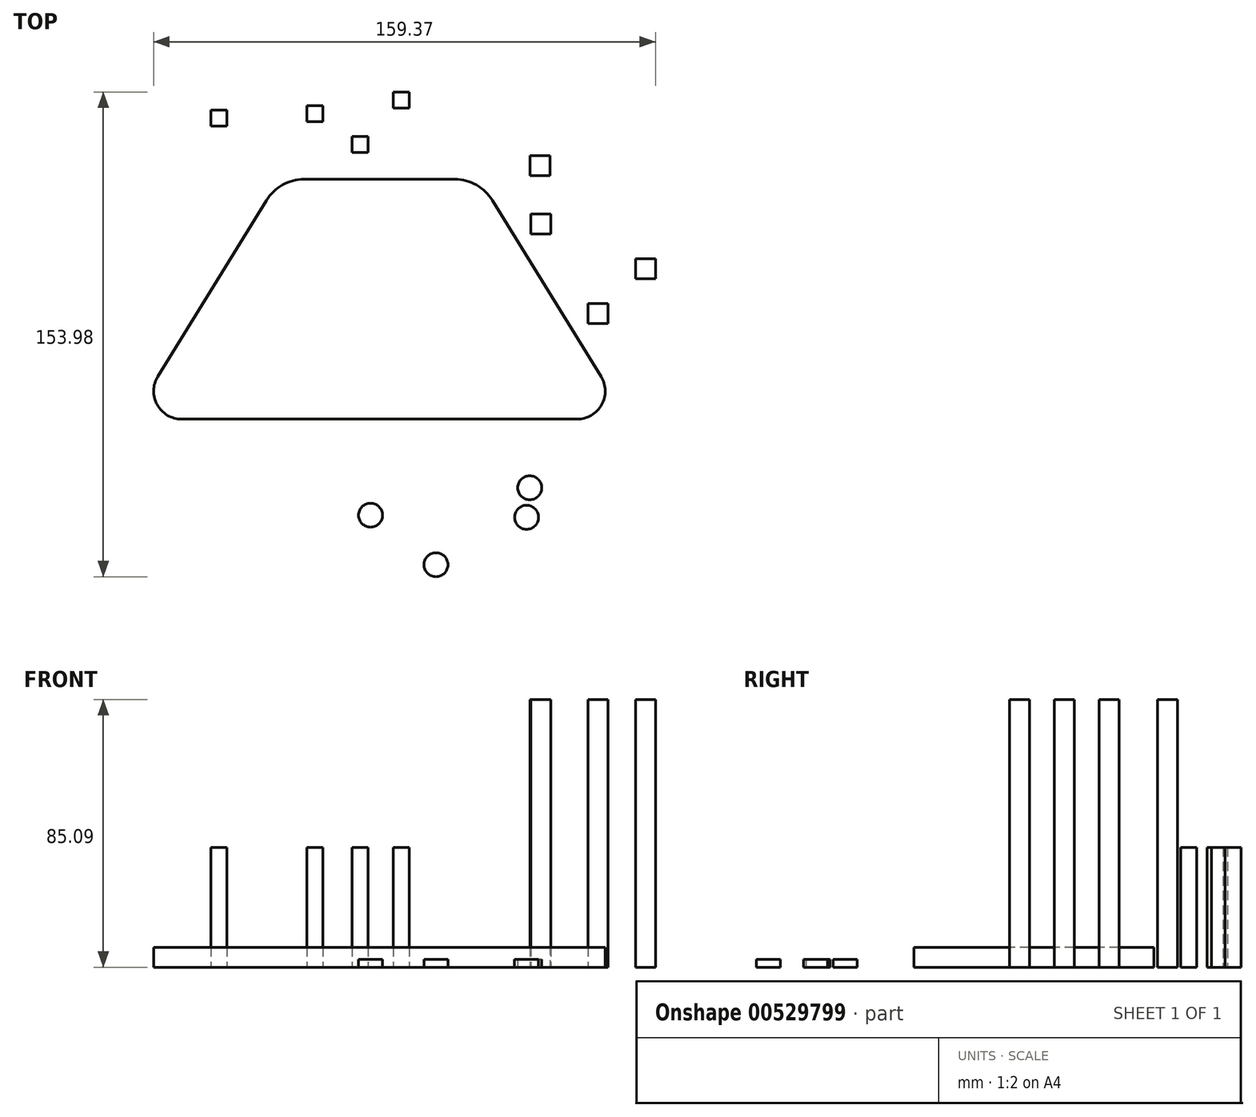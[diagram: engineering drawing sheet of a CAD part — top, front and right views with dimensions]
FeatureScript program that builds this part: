
annotation { "Feature Type Name" : "Feature", "Feature Type Description" : "" }
export const myFeature = defineFeature(function(context is Context, id is Id, definition is map)
    precondition{}
    {
        {
            var Q0;
            Q0=qCreatedBy(makeId("Top.planeOp"),FACE);
            var sketch = newSketch(context, id + "F0", { "sketchPlane" : qUnion([Q0])});
            skLineSegment(sketch, "E0.bottom", {"start": v(-37.94, 43.8) * mm, "end": v(9.96, 43.8) * mm});
            skLineSegment(sketch, "E0.top", {"start": v(-45.74, -32.4) * mm, "end": v(17.76, -32.4) * mm});
            skLineSegment(sketch, "E0.left", {"start": v(-45.74, 43.8) * mm, "end": v(-45.74, -32.4) * mm});
            skLineSegment(sketch, "E0.right", {"start": v(17.76, 43.8) * mm, "end": v(17.76, -32.4) * mm});
            skLineSegment(sketch, "E1", {"start": v(-45.74, -32.4) * mm, "end": v(-76.8, -32.4) * mm});
            skLineSegment(sketch, "E2", {"start": v(17.76, -32.4) * mm, "end": v(48.82, -32.4) * mm});
            skLineSegment(sketch, "E3", {"start": v(-49.83, 37.15) * mm, "end": v(-84.37, -18.85) * mm});
            skLineSegment(sketch, "E4", {"start": v(21.85, 37.15) * mm, "end": v(56.39, -18.85) * mm});
            skPoint(sketch, "E5.visualSharp", {"position": v(-45.74, 43.8) * mm});
            skArc(sketch, "E5.filletArc", {"start": v(-37.94, 43.8) * mm, "mid": v(-44.75, 42.02) * mm, "end": v(-49.83, 37.15) * mm});
            skPoint(sketch, "E6.visualSharp", {"position": v(17.76, 43.8) * mm});
            skArc(sketch, "E6.filletArc", {"start": v(21.85, 37.15) * mm, "mid": v(16.77, 42.02) * mm, "end": v(9.96, 43.8) * mm});
            skPoint(sketch, "E7.visualSharp", {"position": v(-92.73, -32.4) * mm});
            skArc(sketch, "E7.filletArc", {"start": v(-84.37, -18.85) * mm, "mid": v(-84.57, -27.85) * mm, "end": v(-76.8, -32.4) * mm});
            skPoint(sketch, "E8.visualSharp", {"position": v(64.75, -32.4) * mm});
            skArc(sketch, "E8.filletArc", {"start": v(48.82, -32.4) * mm, "mid": v(56.58, -27.85) * mm, "end": v(56.39, -18.85) * mm});
            skSolve(sketch);
        }
        {
            var Q0;
            {var subQ4=sQuery(id+"F0.wireOp",EDGE,"E1");Q0=makeQuery(id+"F0.imprint","IMPRINT",FACE,{"disambiguationData":[TD([[makeQuery(id+"F0.imprint","IMPRINT",EDGE,{"derivedFrom":subQ4}),-1.0]])]});}
            var Q1;
            {var subQ4=sQuery(id+"F0.wireOp",EDGE,"E2");Q1=makeQuery(id+"F0.imprint","IMPRINT",FACE,{"disambiguationData":[TD([[makeQuery(id+"F0.imprint","IMPRINT",EDGE,{"derivedFrom":subQ4}),1.0]])]});}
            var Q2;
            {var subQ7=sQuery(id+"F0.wireOp",EDGE,"E0.bottom");Q2=makeQuery(id+"F0.imprint","IMPRINT",FACE,{"disambiguationData":[TD([[makeQuery(id+"F0.imprint","IMPRINT",EDGE,{"derivedFrom":subQ7}),-1.0]])]});}
            extrude(context, id + "F1", {"entities" : qUnion([Q0, Q1, Q2]), "depth" : 6.35 * mm, "offsetDistance" : 25.4 * mm});
        }
        {
            var Q0;
            Q0=qCreatedBy(makeId("Top.planeOp"),FACE);
            var sketch = newSketch(context, id + "F2", { "sketchPlane" : qUnion([Q0])});
            skLineSegment(sketch, "E9.bottom", {"start": v(40.24, 44.97) * mm, "end": v(33.9, 44.97) * mm});
            skLineSegment(sketch, "E9.top", {"start": v(40.24, 51.32) * mm, "end": v(33.9, 51.32) * mm});
            skLineSegment(sketch, "E9.left", {"start": v(40.24, 44.97) * mm, "end": v(40.24, 51.32) * mm});
            skLineSegment(sketch, "E9.right", {"start": v(33.9, 44.97) * mm, "end": v(33.9, 51.32) * mm});
            skPoint(sketch, "E9.middle", {"position": v(37.07, 48.15) * mm});
            skLineSegment(sketch, "E10.bottom", {"start": v(52.2, 4.3) * mm, "end": v(58.55, 4.3) * mm});
            skLineSegment(sketch, "E10.top", {"start": v(52.2, -2.04) * mm, "end": v(58.55, -2.04) * mm});
            skLineSegment(sketch, "E10.left", {"start": v(52.2, 4.3) * mm, "end": v(52.2, -2.04) * mm});
            skLineSegment(sketch, "E10.right", {"start": v(58.55, 4.3) * mm, "end": v(58.55, -2.04) * mm});
            skPoint(sketch, "E10.middle", {"position": v(55.37, 1.13) * mm});
            skLineSegment(sketch, "E11.bottom", {"start": v(40.4, 26.4) * mm, "end": v(34.04, 26.4) * mm});
            skLineSegment(sketch, "E11.top", {"start": v(40.4, 32.75) * mm, "end": v(34.04, 32.75) * mm});
            skLineSegment(sketch, "E11.left", {"start": v(40.4, 26.4) * mm, "end": v(40.4, 32.75) * mm});
            skLineSegment(sketch, "E11.right", {"start": v(34.04, 26.4) * mm, "end": v(34.04, 32.75) * mm});
            skPoint(sketch, "E11.middle", {"position": v(37.22, 29.58) * mm});
            skLineSegment(sketch, "E12.bottom", {"start": v(73.68, 12.18) * mm, "end": v(67.33, 12.18) * mm});
            skLineSegment(sketch, "E12.top", {"start": v(73.68, 18.53) * mm, "end": v(67.33, 18.53) * mm});
            skLineSegment(sketch, "E12.left", {"start": v(73.68, 12.18) * mm, "end": v(73.68, 18.53) * mm});
            skLineSegment(sketch, "E12.right", {"start": v(67.33, 12.18) * mm, "end": v(67.33, 18.53) * mm});
            skPoint(sketch, "E12.middle", {"position": v(70.5, 15.35) * mm});
            skSolve(sketch);
        }
        {
            var Q0;
            Q0=makeQuery(id+"F2.imprint","IMPRINT",FACE,{"disambiguationData":[TD([[makeQuery(id+"F2.imprint","IMPRINT",EDGE,{"derivedFrom":sQuery(id+"F2.wireOp",EDGE,"E10.bottom")}),-1.0]])]});
            var Q1;
            Q1=makeQuery(id+"F2.imprint","IMPRINT",FACE,{"disambiguationData":[TD([[makeQuery(id+"F2.imprint","IMPRINT",EDGE,{"derivedFrom":sQuery(id+"F2.wireOp",EDGE,"E12.bottom")}),-1.0]])]});
            var Q2;
            Q2=makeQuery(id+"F2.imprint","IMPRINT",FACE,{"disambiguationData":[TD([[makeQuery(id+"F2.imprint","IMPRINT",EDGE,{"derivedFrom":sQuery(id+"F2.wireOp",EDGE,"E11.bottom")}),-1.0]])]});
            var Q3;
            Q3=makeQuery(id+"F2.imprint","IMPRINT",FACE,{"disambiguationData":[TD([[makeQuery(id+"F2.imprint","IMPRINT",EDGE,{"derivedFrom":sQuery(id+"F2.wireOp",EDGE,"E9.bottom")}),-1.0]])]});
            extrude(context, id + "F3", {"entities" : qUnion([Q0, Q1, Q2, Q3]), "depth" : 85.1 * mm, "offsetDistance" : 25.4 * mm});
        }
        {
            var Q0;
            Q0=qCreatedBy(makeId("Top.planeOp"),FACE);
            var sketch = newSketch(context, id + "F4", { "sketchPlane" : qUnion([Q0])});
            skLineSegment(sketch, "E13.bottom", {"start": v(-67.48, 60.73) * mm, "end": v(-62.4, 60.73) * mm});
            skLineSegment(sketch, "E13.top", {"start": v(-67.48, 65.81) * mm, "end": v(-62.4, 65.81) * mm});
            skLineSegment(sketch, "E13.left", {"start": v(-67.48, 60.73) * mm, "end": v(-67.48, 65.81) * mm});
            skLineSegment(sketch, "E13.right", {"start": v(-62.4, 60.73) * mm, "end": v(-62.4, 65.81) * mm});
            skPoint(sketch, "E13.middle", {"position": v(-64.94, 63.27) * mm});
            skLineSegment(sketch, "E14.bottom", {"start": v(-37.08, 62.07) * mm, "end": v(-32, 62.07) * mm});
            skLineSegment(sketch, "E14.top", {"start": v(-37.08, 67.15) * mm, "end": v(-32, 67.15) * mm});
            skLineSegment(sketch, "E14.left", {"start": v(-37.08, 62.07) * mm, "end": v(-37.08, 67.15) * mm});
            skLineSegment(sketch, "E14.right", {"start": v(-32, 62.07) * mm, "end": v(-32, 67.15) * mm});
            skPoint(sketch, "E14.middle", {"position": v(-34.54, 64.61) * mm});
            skLineSegment(sketch, "E15.bottom", {"start": v(-9.63, 66.42) * mm, "end": v(-4.55, 66.42) * mm});
            skLineSegment(sketch, "E15.top", {"start": v(-9.63, 71.5) * mm, "end": v(-4.55, 71.5) * mm});
            skLineSegment(sketch, "E15.left", {"start": v(-9.63, 66.42) * mm, "end": v(-9.63, 71.5) * mm});
            skLineSegment(sketch, "E15.right", {"start": v(-4.55, 66.42) * mm, "end": v(-4.55, 71.5) * mm});
            skPoint(sketch, "E15.middle", {"position": v(-7.09, 68.96) * mm});
            skLineSegment(sketch, "E16.bottom", {"start": v(-22.68, 52.36) * mm, "end": v(-17.6, 52.36) * mm});
            skLineSegment(sketch, "E16.top", {"start": v(-22.68, 57.44) * mm, "end": v(-17.6, 57.44) * mm});
            skLineSegment(sketch, "E16.left", {"start": v(-22.68, 52.36) * mm, "end": v(-22.68, 57.44) * mm});
            skLineSegment(sketch, "E16.right", {"start": v(-17.6, 52.36) * mm, "end": v(-17.6, 57.44) * mm});
            skPoint(sketch, "E16.middle", {"position": v(-20.14, 54.9) * mm});
            skSolve(sketch);
        }
        {
            var Q0;
            Q0=makeQuery(id+"F4.imprint","IMPRINT",FACE,{"disambiguationData":[TD([[makeQuery(id+"F4.imprint","IMPRINT",EDGE,{"derivedFrom":sQuery(id+"F4.wireOp",EDGE,"E15.bottom")}),1.0]])]});
            var Q1;
            Q1=makeQuery(id+"F4.imprint","IMPRINT",FACE,{"disambiguationData":[TD([[makeQuery(id+"F4.imprint","IMPRINT",EDGE,{"derivedFrom":sQuery(id+"F4.wireOp",EDGE,"E16.bottom")}),1.0]])]});
            var Q2;
            Q2=makeQuery(id+"F4.imprint","IMPRINT",FACE,{"disambiguationData":[TD([[makeQuery(id+"F4.imprint","IMPRINT",EDGE,{"derivedFrom":sQuery(id+"F4.wireOp",EDGE,"E14.bottom")}),1.0]])]});
            var Q3;
            Q3=makeQuery(id+"F4.imprint","IMPRINT",FACE,{"disambiguationData":[TD([[makeQuery(id+"F4.imprint","IMPRINT",EDGE,{"derivedFrom":sQuery(id+"F4.wireOp",EDGE,"E13.bottom")}),1.0]])]});
            extrude(context, id + "F5", {"entities" : qUnion([Q0, Q1, Q2, Q3]), "depth" : 38.1 * mm, "offsetDistance" : 25.4 * mm});
        }
        {
            var Q0;
            Q0=qCreatedBy(makeId("Top.planeOp"),FACE);
            var sketch = newSketch(context, id + "F6", { "sketchPlane" : qUnion([Q0])});
            skCircle(sketch, "E17", {"center": v(33.76, -54.23) * mm, "radius": 3.81 * mm});
            skCircle(sketch, "E18", {"center": v(3.96, -78.67) * mm, "radius": 3.81 * mm});
            skCircle(sketch, "E19", {"center": v(-16.8, -62.94) * mm, "radius": 3.81 * mm});
            skCircle(sketch, "E20", {"center": v(32.75, -63.6) * mm, "radius": 3.81 * mm});
            skSolve(sketch);
        }
        {
            var Q0;
            Q0 = qSketchRegion(id + "F6", true);
            extrude(context, id + "F7", {"entities" : qUnion([Q0]), "depth" : 2.54 * mm, "offsetDistance" : 25.4 * mm});
        }
    });
